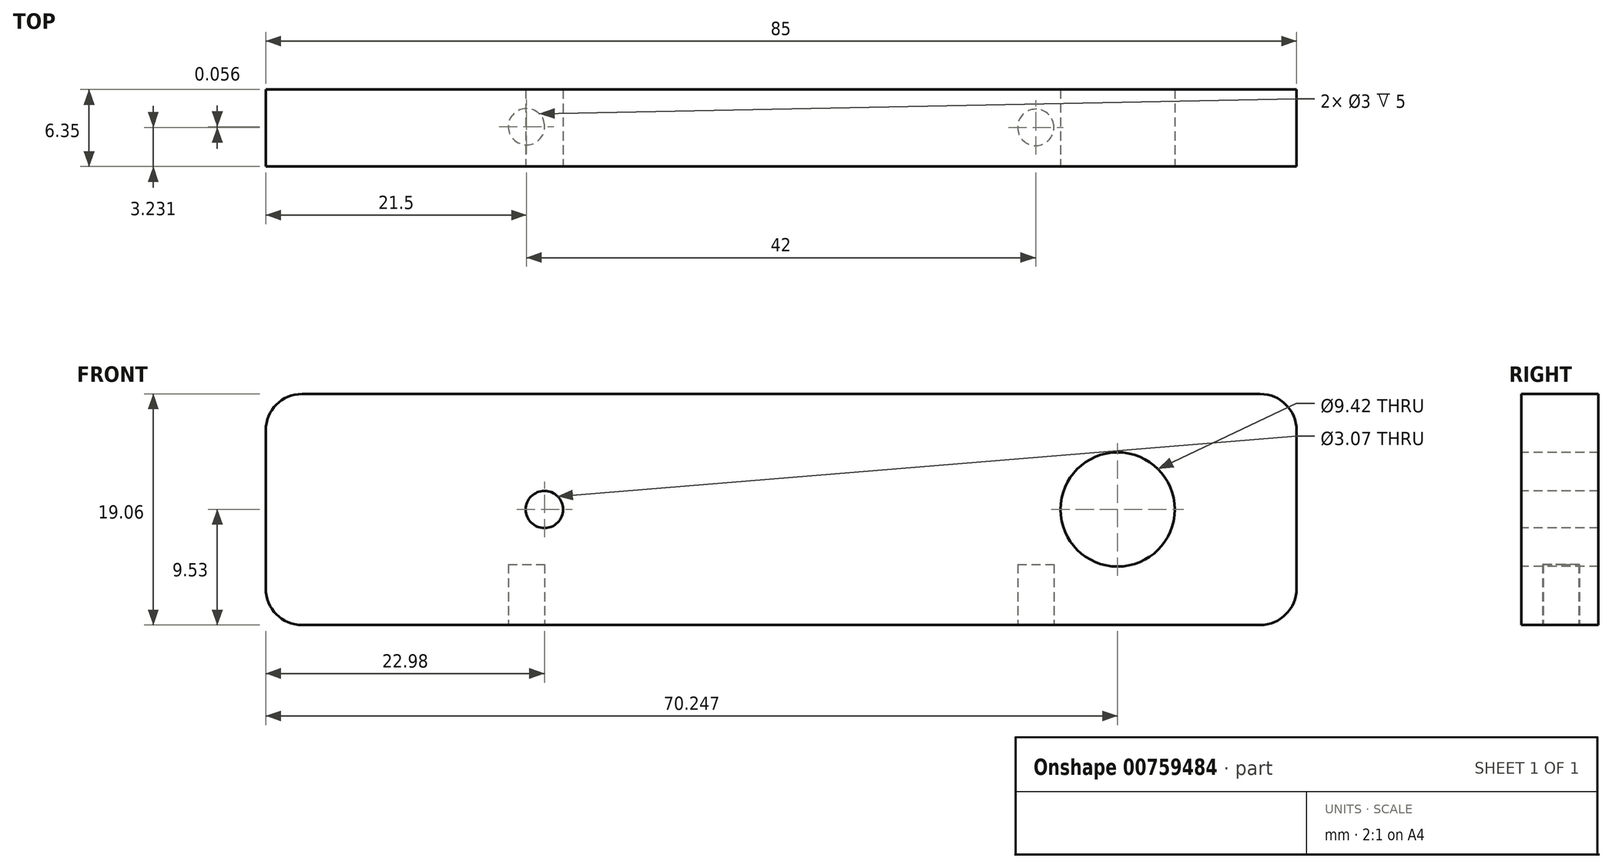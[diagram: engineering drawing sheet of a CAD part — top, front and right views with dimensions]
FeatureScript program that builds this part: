
annotation { "Feature Type Name" : "Feature", "Feature Type Description" : "" }
export const myFeature = defineFeature(function(context is Context, id is Id, definition is map)
    precondition{}
    {
        {
            var Q0;
            Q0=qCreatedBy(makeId("Front.planeOp"),FACE);
            var sketch = newSketch(context, id + "F0", { "sketchPlane" : qUnion([Q0])});
            skLineSegment(sketch, "E0.bottom", {"start": v(-42.5, 9.53) * mm, "end": v(42.5, 9.53) * mm});
            skLineSegment(sketch, "E0.top", {"start": v(-42.5, -9.53) * mm, "end": v(42.5, -9.53) * mm});
            skLineSegment(sketch, "E0.left", {"start": v(-42.5, 9.53) * mm, "end": v(-42.5, -9.53) * mm});
            skLineSegment(sketch, "E0.right", {"start": v(42.5, 9.53) * mm, "end": v(42.5, -9.53) * mm});
            skPoint(sketch, "E0.middle", {"position": v(0, 0) * mm});
            skSolve(sketch);
        }
        {
            var Q0;
            Q0=makeQuery(id+"F0.imprint","IMPRINT",FACE,{"disambiguationData":[TD([[makeQuery(id+"F0.imprint","IMPRINT",EDGE,{"derivedFrom":sQuery(id+"F0.wireOp",EDGE,"E0.bottom")}),-1.0]])]});
            extrude(context, id + "F1", {"entities" : qUnion([Q0]), "depth" : 6.35 * mm, "offsetDistance" : 25 * mm});
        }
        {
            var Q0;
            Q0=makeQuery(id+"F1.opExtrude","SWEPT_EDGE",EDGE,{"disambiguationData":[OSD([sQuery(id+"F0.wireOp",EDGE,"E0.bottom"),sQuery(id+"F0.wireOp",EDGE,"E0.left")])]});
            var Q1;
            Q1=makeQuery(id+"F1.opExtrude","SWEPT_EDGE",EDGE,{"disambiguationData":[OSD([sQuery(id+"F0.wireOp",EDGE,"E0.bottom"),sQuery(id+"F0.wireOp",EDGE,"E0.right")])]});
            var Q2;
            Q2=makeQuery(id+"F1.opExtrude","SWEPT_EDGE",EDGE,{"disambiguationData":[OSD([sQuery(id+"F0.wireOp",EDGE,"E0.top"),sQuery(id+"F0.wireOp",EDGE,"E0.left")])]});
            var Q3;
            Q3=makeQuery(id+"F1.opExtrude","SWEPT_EDGE",EDGE,{"disambiguationData":[OSD([sQuery(id+"F0.wireOp",EDGE,"E0.top"),sQuery(id+"F0.wireOp",EDGE,"E0.right")])]});
            fillet(context, id + "F2", {"entities" : qUnion([Q0, Q1, Q2, Q3]), "radius" : 3 * mm, "tangentPropagation" : true, "allowEdgeOverflow" : false});
        }
        {
            var Q0;
            Q0=makeQuery(id+"F1.opExtrude","CAP_FACE",FACE,{"disambiguationData":[OSD([sQuery(id+"F0.wireOp",EDGE,"E0.bottom"),sQuery(id+"F0.wireOp",EDGE,"E0.top"),sQuery(id+"F0.wireOp",EDGE,"E0.left"),sQuery(id+"F0.wireOp",EDGE,"E0.right")])],"isStart":false});
            var sketch = newSketch(context, id + "F3", { "sketchPlane" : qUnion([Q0])});
            skCircle(sketch, "E1", {"center": v(-19.52, 0) * mm, "radius": 1.54 * mm});
            skCircle(sketch, "E2", {"center": v(27.75, 0) * mm, "radius": 4.7 * mm});
            skSolve(sketch);
        }
        {
            var Q0;
            Q0=makeQuery(id+"F3.imprint","IMPRINT",FACE,{"disambiguationData":[TD([[makeQuery(id+"F3.imprint","IMPRINT",EDGE,{"derivedFrom":sQuery(id+"F3.wireOp",EDGE,"E1")}),1.0]])]});
            var Q1;
            Q1=makeQuery(id+"F3.imprint","IMPRINT",FACE,{"disambiguationData":[TD([[makeQuery(id+"F3.imprint","IMPRINT",EDGE,{"derivedFrom":sQuery(id+"F3.wireOp",EDGE,"E2")}),1.0]])]});
            extrude(context, id + "F4", {"entities" : qUnion([Q0, Q1]), "operationType" : NewBodyOperationType.REMOVE, "oppositeDirection" : true, "depth" : 25 * mm, "offsetDistance" : 25 * mm});
        }
        {
            var Q0;
            Q0=makeQuery(id+"F1.opExtrude","SWEPT_FACE",FACE,{"disambiguationData":[OSD([sQuery(id+"F0.wireOp",EDGE,"E0.top")])]});
            var sketch = newSketch(context, id + "F5", { "sketchPlane" : qUnion([Q0])});
            skCircle(sketch, "E3", {"center": v(21, 3.12) * mm, "radius": 1.5 * mm});
            skCircle(sketch, "E4", {"center": v(-21, 3.06) * mm, "radius": 1.5 * mm});
            skSolve(sketch);
        }
        {
            var Q0;
            Q0=makeQuery(id+"F5.imprint","IMPRINT",FACE,{"disambiguationData":[TD([[makeQuery(id+"F5.imprint","IMPRINT",EDGE,{"derivedFrom":sQuery(id+"F5.wireOp",EDGE,"E4")}),1.0]])]});
            var Q1;
            Q1=makeQuery(id+"F5.imprint","IMPRINT",FACE,{"disambiguationData":[TD([[makeQuery(id+"F5.imprint","IMPRINT",EDGE,{"derivedFrom":sQuery(id+"F5.wireOp",EDGE,"E3")}),1.0]])]});
            extrude(context, id + "F6", {"entities" : qUnion([Q0, Q1]), "operationType" : NewBodyOperationType.REMOVE, "oppositeDirection" : true, "depth" : 5 * mm, "offsetDistance" : 25 * mm});
        }
    });
